# Revit family: Doors_Industrial_Wayne-Dalton_Wind-Load-Roll-Up-Sheet-Doors-Model-790-CW
name_source: partatom
category: Specialty Equipment
units: mm (PartAtom-declared; Revit-internal decimal feet)

## family parameters
Always vertical = Yes
Classification Number = 23.30.10.21.34
Cut with Voids When Loaded = No
Enable Cutting in Views = No
Host = Wall
Maintain Annotation Orientation = No
Part Type = Normal
Room Calculation Point = No
Round Connector Dimension = Use Diameter
Shared = No

## types (5) — shared parameters
Default Elevation = 0"
Description = MODEL 790CW COMMERCIAL WINDLOAD SHEET DOOR
Finish Material = Metal - Wayne Dalton - Galvanized Steel
Manufacturer = Wayne Dalton
Model = 790CW
Number of Poles = 1
Power Factor = 1
Product Guid = 45e5e410-d0bf-4ab5-9bc7-2935a101f9e6
Product Page URL = https://www.wayne-dalton.com
Product data url = https://www.bimobject.com
Slat Height = 10"
URL = https://www.wayne-dalton.com
Wall Closure = By host

## per-type parameters (varying)
| type | Apparent Load Phase 1 | Current | Electrical Operator | Frequency | Voltage |
| ‏​Manual push-up | 0 VA | 0 A | No | 0 Hz | 0 V |
| Chain Hoist | 0 VA | 0 A | No | 0 Hz | 0 V |
| 115 volts, one phase, 60 Hz (110-120V range) | 2300 VA | 20 A | Yes | 60 Hz | 115 V |
| 208 volts, one phase, 60 Hz (190-207V range) | 4160 VA | 20 A | Yes | 60 Hz | 208 V |
| 230 volts, one phase, 60 Hz (208-245V range) | 4600 VA | 20 A | Yes | 60 Hz | 230 V |

type visibility flags (boolean, named after types; folded from table):
- ‏​Manual push-up: Yes: (none)
- Chain Hoist: Yes: Chain Hoist
- 115 volts, one phase, 60 Hz (110-120V range): Yes: (none)
- 208 volts, one phase, 60 Hz (190-207V range): Yes: (none)
- 230 volts, one phase, 60 Hz (208-245V range): Yes: (none)

## geometry (parser evidence)
native form markers: Sweep x10
no freeform markers — native parametric forms only
